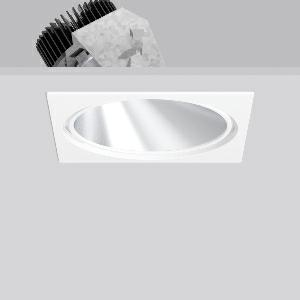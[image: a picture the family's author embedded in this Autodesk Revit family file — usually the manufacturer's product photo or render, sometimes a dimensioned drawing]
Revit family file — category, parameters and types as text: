
# Revit family: pascala_square_901806_002_2507
name_source: partatom
category: Lighting Fixtures
units: mm (PartAtom-declared; Revit-internal decimal feet)

## family parameters
Cut with Voids When Loaded = No
Host = Face
Light Source = No
Part Type = Normal
Room Calculation Point = No
Round Connector Dimension = Use Diameter
Shared = No

## types (1)
- MultiLumen 1 (1 x LED Modul 930, 1700 lm, 3000)
    Apparent Load = 11 VA
    Approval mark = CE
    CIE Flux Codes = 74 99 100 100 100
    Color Rendering = 90
    Color Temperature = 3000
    Default Elevation = 1800 mm
    Description = Series: PASCALA square
High quality recessed downlight. Mounting bracket: galvanised sheet steel. Inner ring and square cover plate: die-cast aluminium. Brilliantly luminous corona at the light-emitting surfaces thanks to use of a specially designed cast aluminium ring as a reflector closure. Reflector material: MIRO-SILVER with 98 percent total light reflection. Patented round design shaped like a truncated cone. MultiLumen: 16 different luminous fluxes can be set on site in approx. 200 lm steps using DIP switches on the separate converter. Installation without tools thanks to spring fastening system. Suitable for through-wiring with separately available accessories. Through-wiring box (5 pole) available as accessory. 
Colour: traffic white, matt (RAL 9016)
Length: 242 mm
Width: 242 mm
Height: 3 mm
Cut-out diameter: 228 mm
Recess height: 175 mm
Luminaire: recess height: 172 mm
Lamp: LED
Socket: without socket
Colour temperature: 3000K
Colour rendering index (CRI): 92
System power: 11 W
Rated luminous flux: 1700 lm
Luminous efficiency: 155 lm/W
System power 2: 19 W
Rated luminous flux 2: 2650 lm
Luminous efficiency 2: 139 lm/W
System power 3: 26 W
Rated luminous flux 3: 3500 lm
Luminous efficiency 3: 135 lm/W
System power 4: 39 W
Rated luminous flux 4: 5000 lm
Luminous efficiency 4: 128 lm/W
Control gear: Regulated power supply
Protection class: II
Type of protection: IP 20
    Height = 0 mm  [stored 0 ft]
    Lamp = 1 x LED Modul 930
    Lamp Light Flux = 1700 lm
    Lamp count = 1
    Length = 242 mm
    Lifetime = 50000 h
    Luminous efficacy = 155 lm/W
    Manufacturer = RZB
    ModVariant = No
    Model = 901806.002
    Mounting Place = Ceiling
    Mounting Type = Recessed
    Number of Poles = 1
    OnlyDefault = Yes
    Power Factor = 1
    Product Name = PASCALA square
    Product group = Recessed downlights
    ProductGroupID = 402
    Protection Class = Protection class II
    Protection Degree = IP 20
    RLX_Detail_Level = 1
    RLX_Emergency_Light_Flux = 0 lm
    RLX_Emergency_Type = 0
    RLX_Emergency_Type_DB = No
    RlxData = <blob elided: 74233 chars, md5=97cf49ec>
    Socket = socket
    Standby Power = 0 W
    System Light Flux = 1700 lm
    System Power = 11 W
    Type Comments = MultiLumen 1
    Type Image = 901567.002.jpg
    URL = http://relux.com
    VarID = multilumen_1
    Voltage = 230 V
    Voltage Range = 220-240 V
    Weight = 0.00 kg
    Width = 242 mm

note: [stored X ft] marks values corroborated as IEEE doubles in the binary element streams (Revit-internal decimal feet)

## geometry (parser evidence)
native form markers: Blend x4, Sweep x9
no freeform markers — native parametric forms only
